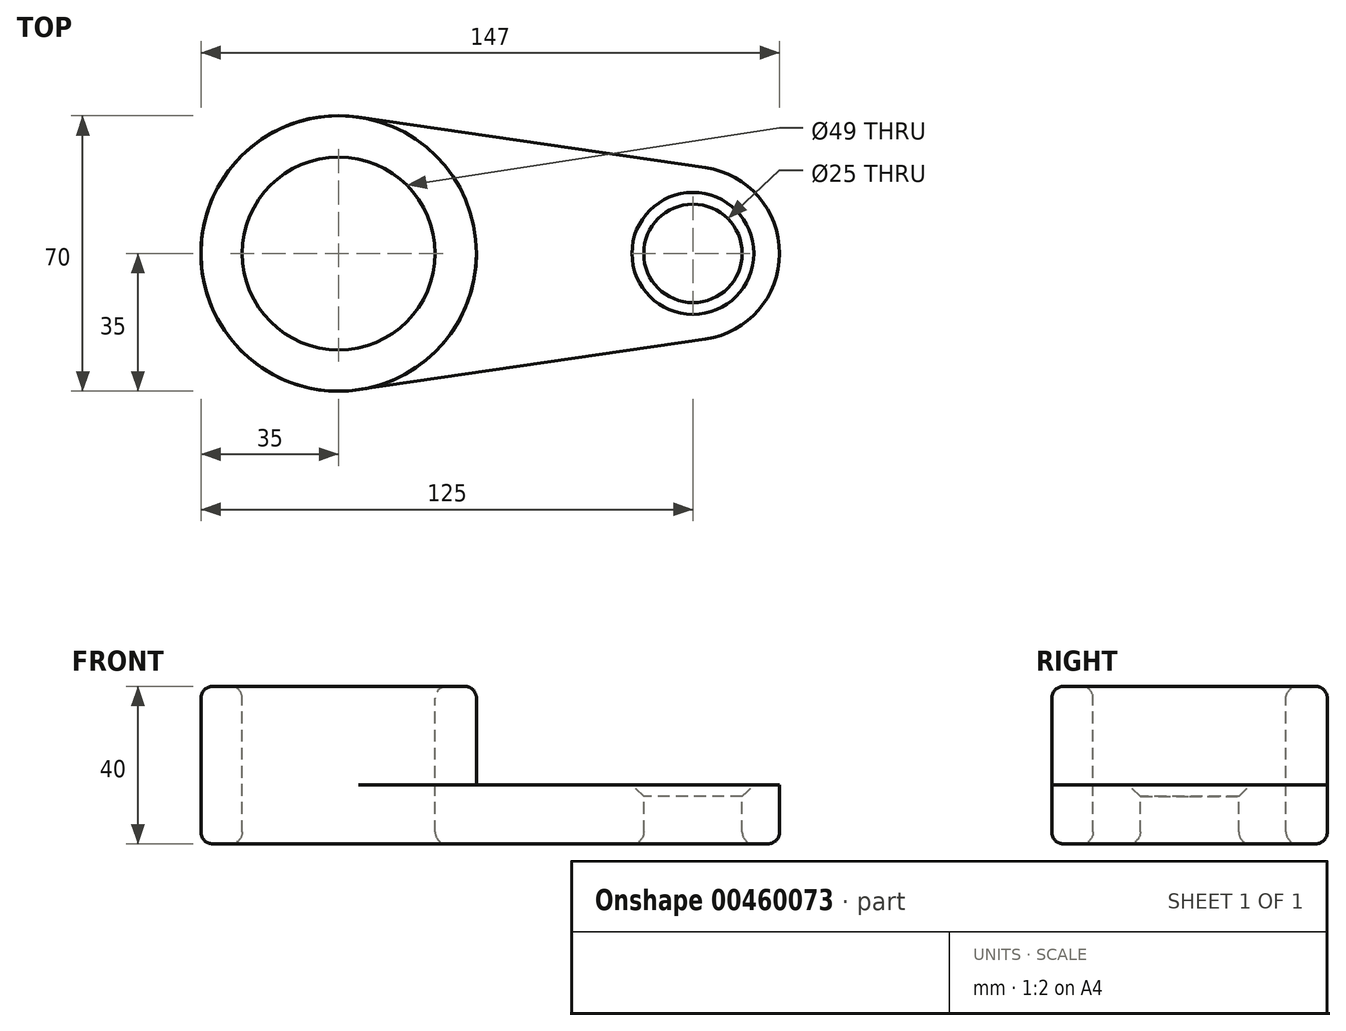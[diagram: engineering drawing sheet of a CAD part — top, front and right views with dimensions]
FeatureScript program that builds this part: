
annotation { "Feature Type Name" : "Feature", "Feature Type Description" : "" }
export const myFeature = defineFeature(function(context is Context, id is Id, definition is map)
    precondition{}
    {
        {
            var Q0;
            Q0=qCreatedBy(makeId("Top.planeOp"),FACE);
            var sketch = newSketch(context, id + "F0", { "sketchPlane" : qUnion([Q0])});
            skLineSegment(sketch, "E0", {"start": v(5.06, 34.63) * mm, "end": v(93.18, 21.77) * mm});
            skLineSegment(sketch, "E1", {"start": v(93.18, -21.77) * mm, "end": v(5.06, -34.63) * mm});
            skCircle(sketch, "E2", {"center": v(0, 0) * mm, "radius": 24.5 * mm});
            skCircle(sketch, "E3", {"center": v(90, 0) * mm, "radius": 12.5 * mm});
            skCircle(sketch, "E4.converted", {"center": v(0, 0) * mm, "radius": 35 * mm});
            skCircle(sketch, "E5.converted", {"center": v(90, 0) * mm, "radius": 22 * mm});
            skSolve(sketch);
        }
        {
            var Q0;
            Q0=makeQuery(id+"F0.imprint","IMPRINT",FACE,{"disambiguationData":[TD([[makeQuery(id+"F0.imprint","IMPRINT",EDGE,{"derivedFrom":sQuery(id+"F0.wireOp",EDGE,"ezXLFuHs-fuf6-m7Fw-qr7c-kFfQBWvX6Fhn")}),1.0]])]});
            var Q1;
            Q1=makeQuery(id+"F0.imprint","IMPRINT",FACE,{"disambiguationData":[TD([[makeQuery(id+"F0.imprint","IMPRINT",EDGE,{"derivedFrom":sQuery(id+"F0.wireOp",EDGE,"E2")}),-1.0]])]});
            var Q2;
            {var subQ0=sQuery(id+"F0.wireOp",EDGE,"E0");Q2=makeQuery(id+"F0.imprint","IMPRINT",FACE,{"disambiguationData":[TD([[makeQuery(id+"F0.imprint","IMPRINT",EDGE,{"derivedFrom":subQ0}),-1.0]])]});}
            var Q3;
            Q3=makeQuery(id+"F0.imprint","IMPRINT",FACE,{"disambiguationData":[TD([[makeQuery(id+"F0.imprint","IMPRINT",EDGE,{"derivedFrom":sQuery(id+"F0.wireOp",EDGE,"E3")}),-1.0]])]});
            extrude(context, id + "F1", {"entities" : qUnion([Q0, Q1, Q2, Q3]), "oppositeDirection" : true, "depth" : 15 * mm});
        }
        {
            var Q0;
            Q0=makeQuery(id+"F0.imprint","IMPRINT",FACE,{"disambiguationData":[TD([[makeQuery(id+"F0.imprint","IMPRINT",EDGE,{"derivedFrom":sQuery(id+"F0.wireOp",EDGE,"E2")}),-1.0]])]});
            extrude(context, id + "F2", {"entities" : qUnion([Q0]), "operationType" : NewBodyOperationType.ADD, "depth" : 25 * mm});
        }
        {
            var Q0;
            Q0=makeQuery(id+"F2.opExtrude","CAP_EDGE",EDGE,{"disambiguationData":[OSD([sQuery(id+"F0.wireOp",EDGE,"E4.converted")])],"isStart":false});
            var Q1;
            Q1=makeQuery(id+"F2.opExtrude","CAP_EDGE",EDGE,{"disambiguationData":[OSD([sQuery(id+"F0.wireOp",EDGE,"E2")])],"isStart":false});
            var Q2;
            Q2=makeQuery(id+"F1.opExtrude","CAP_FACE",FACE,{"disambiguationData":[OSD([sQuery(id+"F0.wireOp",EDGE,"E0"),sQuery(id+"F0.wireOp",EDGE,"E1"),sQuery(id+"F0.wireOp",EDGE,"E2"),sQuery(id+"F0.wireOp",EDGE,"E3"),sQuery(id+"F0.wireOp",EDGE,"E4.converted"),sQuery(id+"F0.wireOp",EDGE,"E5.converted")])],"isStart":false});
            fillet(context, id + "F3", {"entities" : qUnion([Q0, Q1, Q2]), "radius" : 3 * mm, "tangentPropagation" : true, "allowEdgeOverflow" : false});
        }
        {
            var Q0;
            Q0=makeQuery(id+"F1.opExtrude","CAP_EDGE",EDGE,{"disambiguationData":[OSD([sQuery(id+"F0.wireOp",EDGE,"E3")])],"isStart":true});
            chamfer(context, id + "F4", {"entities" : qUnion([Q0]), "width" : 3 * mm, "tangentPropagation" : true});
        }
    });
